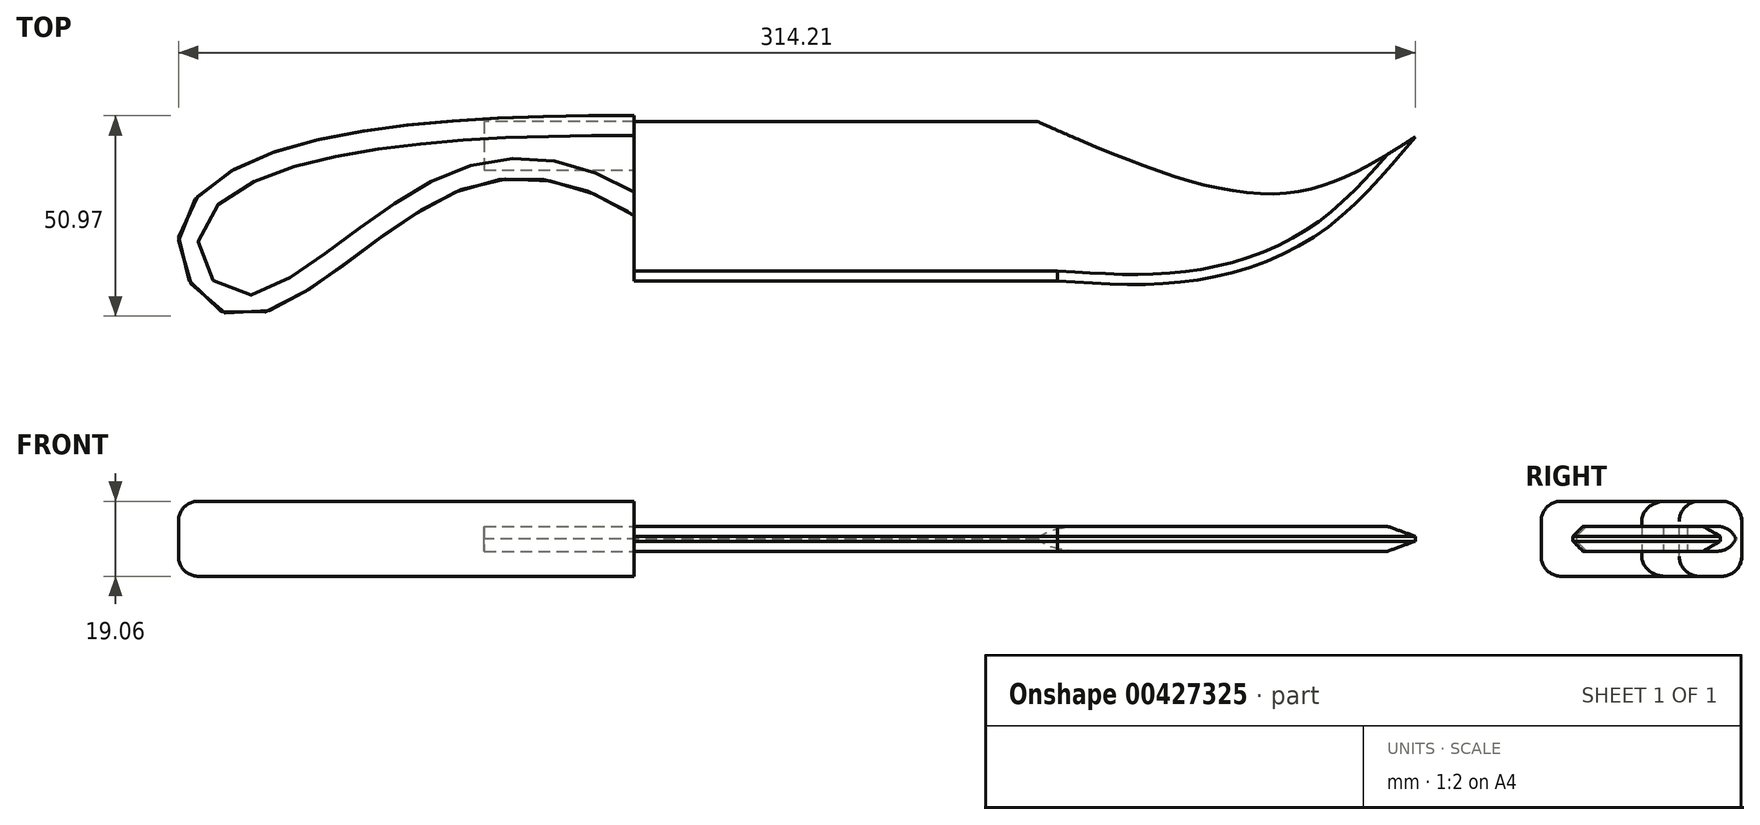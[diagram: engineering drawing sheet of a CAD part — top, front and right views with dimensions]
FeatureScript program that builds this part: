
annotation { "Feature Type Name" : "Feature", "Feature Type Description" : "" }
export const myFeature = defineFeature(function(context is Context, id is Id, definition is map)
    precondition{}
    {
        {
            var Q0;
            Q0=qCreatedBy(makeId("Top.planeOp"),FACE);
            var sketch = newSketch(context, id + "F0", { "sketchPlane" : qUnion([Q0])});
            skLineSegment(sketch, "E0", {"start": v(-72.6, 4.26) * mm, "end": v(-72.6, -8.44) * mm});
            skLineSegment(sketch, "E1", {"start": v(-72.6, -8.44) * mm, "end": v(-34.5, -8.44) * mm});
            skLineSegment(sketch, "E2", {"start": v(-34.5, -8.44) * mm, "end": v(-34.5, 4.26) * mm});
            skLineSegment(sketch, "E3", {"start": v(-72.6, 4.26) * mm, "end": v(-34.5, 4.26) * mm});
            skLineSegment(sketch, "E4", {"start": v(-34.5, 4.26) * mm, "end": v(67.1, 4.26) * mm});
            skLineSegment(sketch, "E5", {"start": v(-34.5, -8.44) * mm, "end": v(-34.5, -36.6) * mm});
            skLineSegment(sketch, "E6", {"start": v(-34.5, -36.6) * mm, "end": v(73.01, -36.6) * mm});
            skFitSpline(sketch, "E7", {"points": [v(73.01, -36.6) * mm, v(107.06, -36.6) * mm, v(139.17, -24.77) * mm, v(163.94, 0) * mm], "startDerivative": vector(102.81, -6.96) * mm, "endDerivative": vector(67.91, 81.48) * mm});
            skFitSpline(sketch, "E8", {"points": [v(163.94, 0) * mm, v(129.1, -14.42) * mm, v(67.1, 4.26) * mm], "startDerivative": vector(-74.25, -47.67) * mm, "endDerivative": vector(-117.48, 51.74) * mm});
            skSolve(sketch);
        }
        {
            var Q0;
            Q0=makeQuery(id+"F0.imprint","IMPRINT",FACE,{"disambiguationData":[TD([[makeQuery(id+"F0.imprint","IMPRINT",EDGE,{"derivedFrom":sQuery(id+"F0.wireOp",EDGE,"E0")}),1.0]])]});
            var Q1;
            Q1=makeQuery(id+"F0.imprint","IMPRINT",FACE,{"disambiguationData":[TD([[makeQuery(id+"F0.imprint","IMPRINT",EDGE,{"derivedFrom":sQuery(id+"F0.wireOp",EDGE,"E2")}),-1.0]])]});
            extrude(context, id + "F1", {"entities" : qUnion([Q0, Q1]), "endBound" : BoundingType.SYMMETRIC, "depth" : 6.35 * mm});
        }
        {
            var Q0;
            Q0=makeQuery(id+"F1.opExtrude","CAP_EDGE",EDGE,{"disambiguationData":[OSD([sQuery(id+"F0.wireOp",EDGE,"E6")])],"isStart":false});
            var Q1;
            Q1=makeQuery(id+"F1.opExtrude","CAP_EDGE",EDGE,{"disambiguationData":[OSD([sQuery(id+"F0.wireOp",EDGE,"E6")])],"isStart":true});
            var Q2;
            Q2=makeQuery(id+"F1.opExtrude","CAP_EDGE",EDGE,{"disambiguationData":[OSD([sQuery(id+"F0.wireOp",EDGE,"6f9b8cad-e21c-4201-b929-6ad18973c9c9")])],"isStart":false});
            var Q3;
            Q3=makeQuery(id+"F1.opExtrude","CAP_EDGE",EDGE,{"disambiguationData":[OSD([sQuery(id+"F0.wireOp",EDGE,"6f9b8cad-e21c-4201-b929-6ad18973c9c9")])],"isStart":true});
            var Q4;
            Q4=makeQuery(id+"F1.opExtrude","CAP_EDGE",EDGE,{"disambiguationData":[OSD([sQuery(id+"F0.wireOp",EDGE,"b08ba592-b06b-44c6-8be9-46baae2555db")])],"isStart":false});
            var Q5;
            Q5=makeQuery(id+"F1.opExtrude","CAP_EDGE",EDGE,{"disambiguationData":[OSD([sQuery(id+"F0.wireOp",EDGE,"b08ba592-b06b-44c6-8be9-46baae2555db")])],"isStart":true});
            chamfer(context, id + "F2", {"entities" : qUnion([Q0, Q1, Q2, Q3, Q4, Q5]), "width" : 2.54 * mm, "tangentPropagation" : true});
        }
        {
            var Q0;
            Q0=makeQuery(id+"F1.opExtrude","CAP_EDGE",EDGE,{"disambiguationData":[OSD([sQuery(id+"F0.wireOp",EDGE,"E3"),sQuery(id+"F0.wireOp",EDGE,"E4")])],"isStart":true});
            var Q1;
            Q1=makeQuery(id+"F1.opExtrude","CAP_EDGE",EDGE,{"disambiguationData":[OSD([sQuery(id+"F0.wireOp",EDGE,"E3"),sQuery(id+"F0.wireOp",EDGE,"E4")])],"isStart":false});
            fillet(context, id + "F3", {"entities" : qUnion([Q0, Q1]), "radius" : 5.08 * mm, "tangentPropagation" : true, "allowEdgeOverflow" : false});
        }
        {
            var Q0;
            Q0=qCreatedBy(makeId("Top.planeOp"),FACE);
            var sketch = newSketch(context, id + "F4", { "sketchPlane" : qUnion([Q0])});
            skLineSegment(sketch, "E9", {"start": v(-34.48, 5.39) * mm, "end": v(-34.48, -20.01) * mm});
            skFitSpline(sketch, "E10", {"points": [v(-34.48, -20.01) * mm, v(-77.83, -13.15) * mm, v(-134.6, -45.55) * mm, v(-150.27, -26.12) * mm, v(-126.18, -3.95) * mm, v(-34.48, 5.39) * mm], "startDerivative": vector(-174.98, 116.4) * mm, "endDerivative": vector(337.45, -1.84) * mm});
            skSolve(sketch);
        }
        {
            var Q0;
            Q0=makeQuery(id+"F4.imprint","IMPRINT",FACE,{"disambiguationData":[TD([[makeQuery(id+"F4.imprint","IMPRINT",EDGE,{"derivedFrom":sQuery(id+"F4.wireOp",EDGE,"E9")}),-1.0]])]});
            extrude(context, id + "F5", {"entities" : qUnion([Q0]), "endBound" : BoundingType.SYMMETRIC, "depth" : 19.05 * mm});
        }
        {
            var Q0;
            Q0=makeQuery(id+"F5.opExtrude","CAP_EDGE",EDGE,{"disambiguationData":[OSD([sQuery(id+"F4.wireOp",EDGE,"E10")])],"isStart":false});
            var Q1;
            Q1=makeQuery(id+"F5.opExtrude","CAP_EDGE",EDGE,{"disambiguationData":[OSD([sQuery(id+"F4.wireOp",EDGE,"E10")])],"isStart":true});
            fillet(context, id + "F6", {"entities" : qUnion([Q0, Q1]), "radius" : 5.08 * mm, "tangentPropagation" : true, "allowEdgeOverflow" : false});
        }
        {
            var Q0;
            Q0=makeQuery(id+"F1.opExtrude","CAP_EDGE",EDGE,{"disambiguationData":[OSD([sQuery(id+"F0.wireOp",EDGE,"E7")])],"isStart":false});
            var Q1;
            Q1=makeQuery(id+"F1.opExtrude","CAP_EDGE",EDGE,{"disambiguationData":[OSD([sQuery(id+"F0.wireOp",EDGE,"E7")])],"isStart":true});
            chamfer(context, id + "F7", {"entities" : qUnion([Q0, Q1]), "width" : 2.54 * mm, "tangentPropagation" : true});
        }
    });
